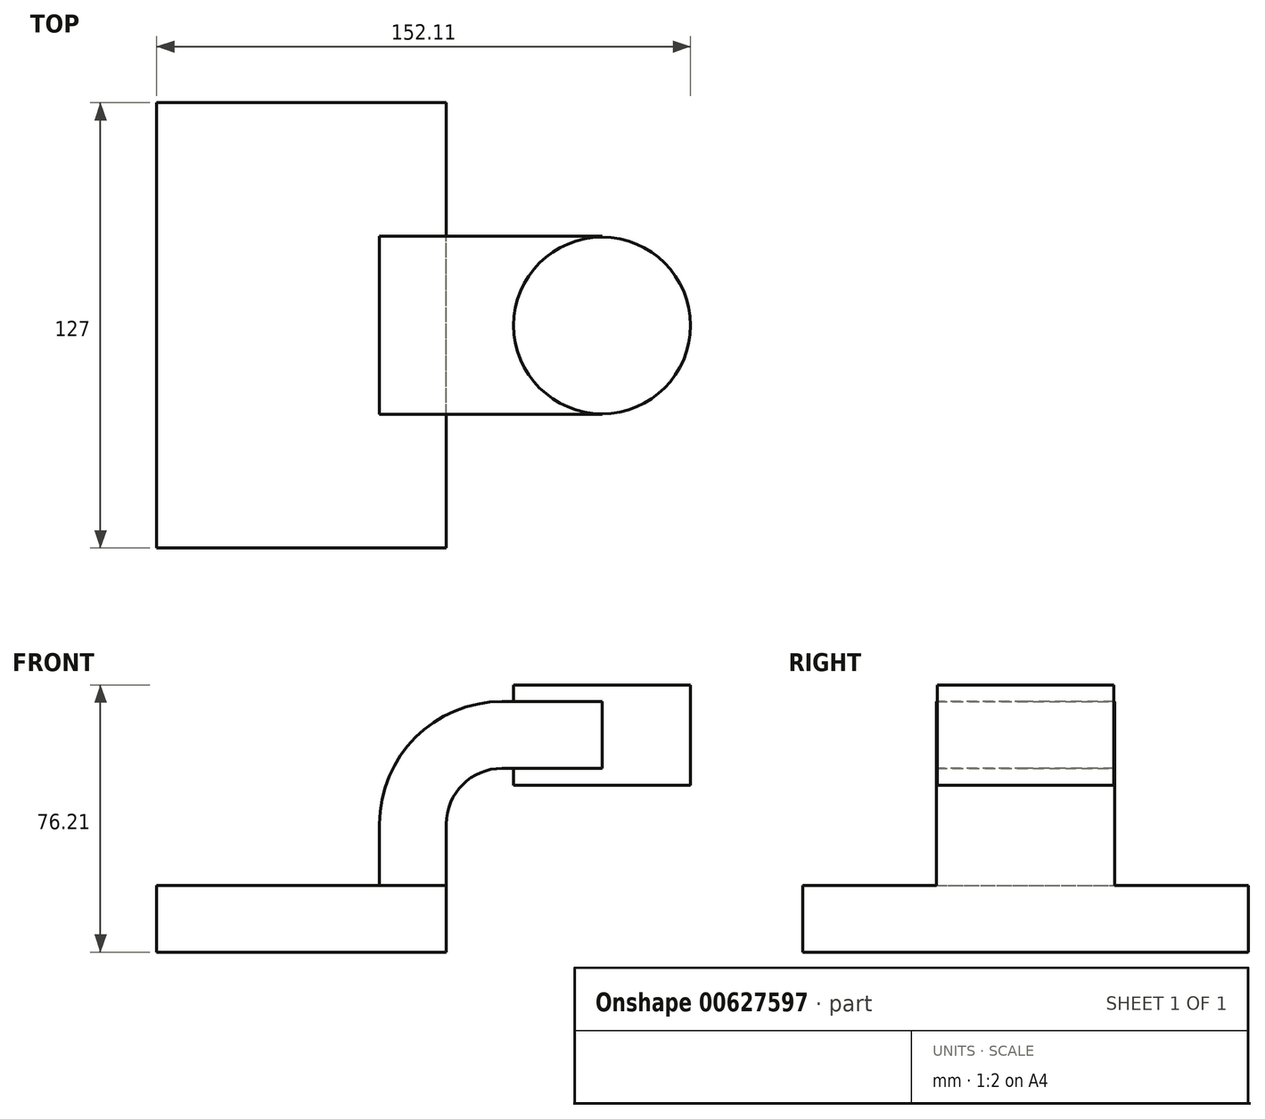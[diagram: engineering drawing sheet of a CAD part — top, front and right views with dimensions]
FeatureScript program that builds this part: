
annotation { "Feature Type Name" : "Feature", "Feature Type Description" : "" }
export const myFeature = defineFeature(function(context is Context, id is Id, definition is map)
    precondition{}
    {
        {
            var Q0;
            Q0=qCreatedBy(makeId("Front.planeOp"),FACE);
            var sketch = newSketch(context, id + "F0", { "sketchPlane" : qUnion([Q0])});
            skLineSegment(sketch, "E0.bottom", {"start": v(-41.28, -9.53) * mm, "end": v(41.28, -9.53) * mm});
            skLineSegment(sketch, "E0.top", {"start": v(-41.28, 9.52) * mm, "end": v(41.28, 9.52) * mm});
            skLineSegment(sketch, "E0.left", {"start": v(-41.28, -9.53) * mm, "end": v(-41.28, 9.52) * mm});
            skLineSegment(sketch, "E0.right", {"start": v(41.28, -9.53) * mm, "end": v(41.28, 9.52) * mm});
            skPoint(sketch, "E0.middle", {"position": v(0, 0) * mm});
            skLineSegment(sketch, "E1.bottom", {"start": v(60.04, 38.1) * mm, "end": v(110.84, 38.1) * mm});
            skLineSegment(sketch, "E1.top", {"start": v(60.04, 66.67) * mm, "end": v(110.84, 66.67) * mm});
            skLineSegment(sketch, "E1.left", {"start": v(60.04, 38.1) * mm, "end": v(60.04, 66.67) * mm});
            skLineSegment(sketch, "E1.right", {"start": v(110.84, 38.1) * mm, "end": v(110.84, 66.67) * mm});
            skPoint(sketch, "E1.middle", {"position": v(85.44, 52.39) * mm});
            skLineSegment(sketch, "E2", {"start": v(41.28, 9.52) * mm, "end": v(41.28, 27) * mm});
            skArc(sketch, "E3", {"start": v(41.27, 27) * mm, "mid": v(45.92, 38.23) * mm, "end": v(57.15, 42.88) * mm});
            skLineSegment(sketch, "E4", {"start": v(57.15, 42.88) * mm, "end": v(85.72, 42.88) * mm});
            skArc(sketch, "E5.1", {"start": v(22.22, 27) * mm, "mid": v(32.45, 51.7) * mm, "end": v(57.15, 61.93) * mm});
            skLineSegment(sketch, "E5.2", {"start": v(22.22, 9.52) * mm, "end": v(22.22, 27) * mm});
            skLineSegment(sketch, "E6", {"start": v(85.65, 38.1) * mm, "end": v(85.65, 66.67) * mm});
            skPoint(sketch, "E6.startSnap0", {"position": v(85.44, 38.1) * mm});
            skPoint(sketch, "E6.startSnap1", {"position": v(85.65, 61.93) * mm});
            skPoint(sketch, "E6.endSnap0", {"position": v(85.44, 66.67) * mm});
            skFitSpline(sketch, "E7", {"points": [v(-41.28, 9.53) * mm, v(57.15, 61.93) * mm], "startDerivative": vector(0, 52.43) * mm, "endDerivative": vector(104.78, 0) * mm});
            skLineSegment(sketch, "E8", {"start": v(57.15, 61.93) * mm, "end": v(85.65, 61.93) * mm});
            skSolve(sketch);
        }
        {
            var Q0;
            Q0=makeQuery(id+"F0.imprint","IMPRINT",FACE,{"disambiguationData":[TD([[makeQuery(id+"F0.imprint","IMPRINT",EDGE,{"derivedFrom":sQuery(id+"F0.wireOp",EDGE,"E0.bottom")}),1.0]])]});
            extrude(context, id + "F1", {"entities" : qUnion([Q0]), "endBound" : BoundingType.SYMMETRIC, "depth" : 127 * mm, "offsetDistance" : 25.4 * mm});
        }
        {
            var Q0;
            {var subQ0=sQuery(id+"F0.wireOp",EDGE,"E4");var subQ1=sQuery(id+"F0.wireOp",EDGE,"E1.left");var subQ2=makeQuery(id+"F0.imprint","INTERSECT",VERTEX,{"derivedFrom":[subQ1,subQ0]});Q0=makeQuery(id+"F0.imprint","IMPRINT",FACE,{"disambiguationData":[TD([[makeQuery(id+"F0.imprint","IMPRINT",EDGE,{"disambiguationData":[TD([[subQ2,-1.0]])],"derivedFrom":subQ1}),-1.0]])]});}
            var Q1;
            {var subQ1=sQuery(id+"F0.wireOp",EDGE,"E2");Q1=makeQuery(id+"F0.imprint","IMPRINT",FACE,{"disambiguationData":[TD([[makeQuery(id+"F0.imprint","IMPRINT",EDGE,{"derivedFrom":subQ1}),1.0]])]});}
            extrude(context, id + "F2", {"entities" : qUnion([Q0, Q1]), "operationType" : NewBodyOperationType.ADD, "endBound" : BoundingType.SYMMETRIC, "depth" : 50.8 * mm, "offsetDistance" : 25.4 * mm});
        }
        {
            var Q0;
            Q0=makeQuery(id+"F0.imprint","IMPRINT",FACE,{"disambiguationData":[TD([[makeQuery(id+"F0.imprint","IMPRINT",EDGE,{"derivedFrom":sQuery(id+"F0.wireOp",EDGE,"E5.1")}),1.0]])]});
            extrude(context, id + "F3", {"entities" : qUnion([Q0]), "operationType" : NewBodyOperationType.ADD, "endBound" : BoundingType.SYMMETRIC, "depth" : 15.88 * mm, "offsetDistance" : 25.4 * mm});
        }
        {
            var Q0;
            {var subQ4=sQuery(id+"F0.wireOp",EDGE,"E1.right");Q0=makeQuery(id+"F0.imprint","IMPRINT",FACE,{"disambiguationData":[TD([[makeQuery(id+"F0.imprint","IMPRINT",EDGE,{"derivedFrom":subQ4}),1.0]])]});}
            var Q1;
            Q1=sQuery(id+"F0.wireOp",EDGE,"E6");
            revolve(context, id + "F4", {"operationType" : NewBodyOperationType.ADD, "entities" : qUnion([Q0]), "axis" : qUnion([Q1]), "revolveType" : RevolveType.FULL});
        }
    });
